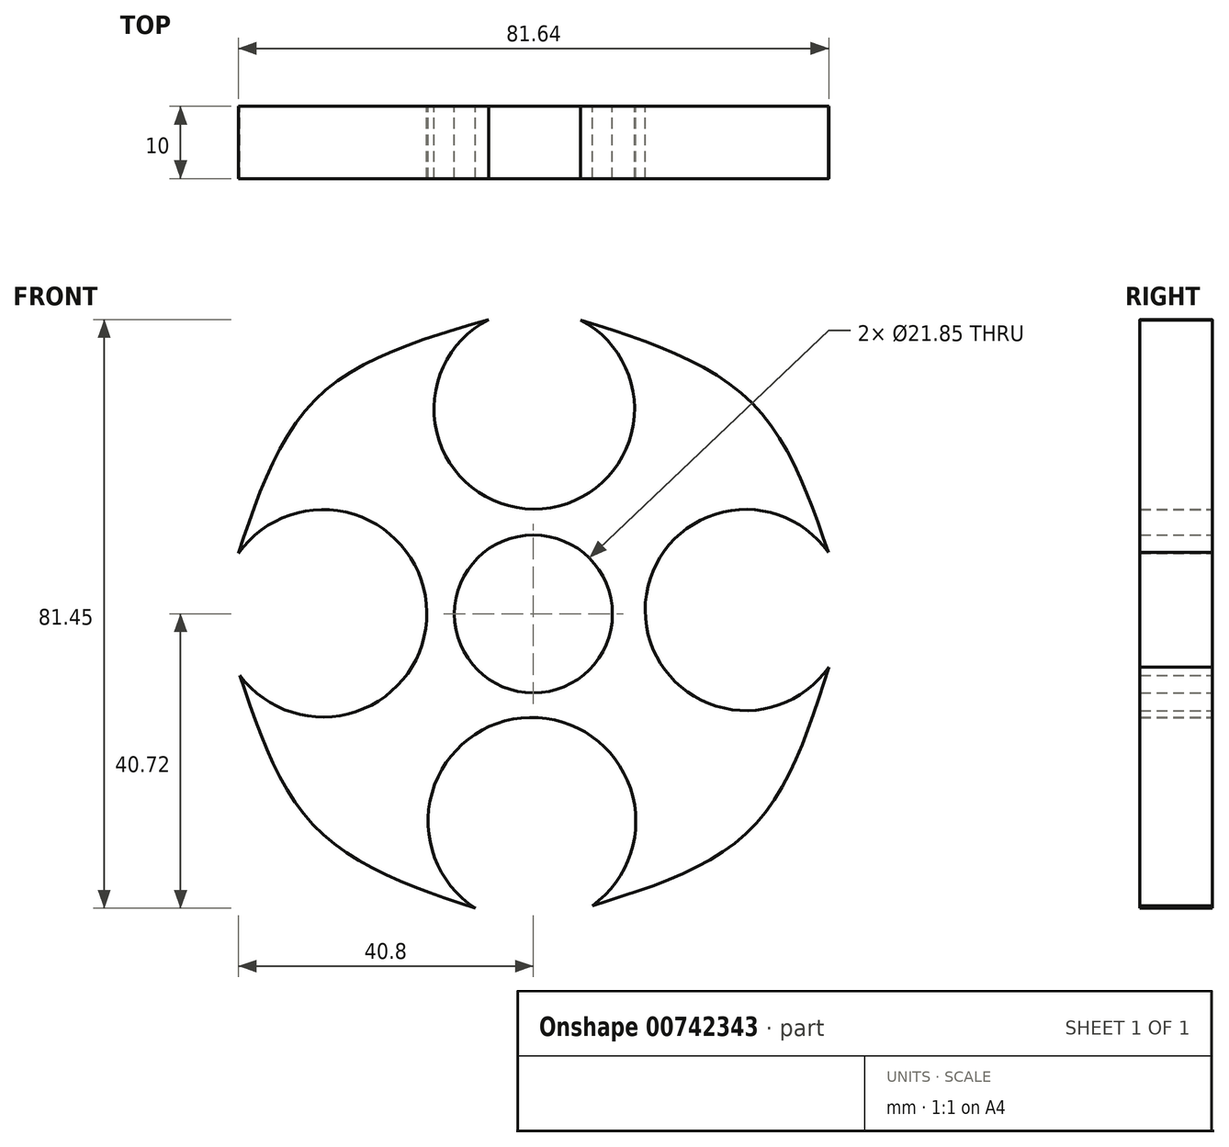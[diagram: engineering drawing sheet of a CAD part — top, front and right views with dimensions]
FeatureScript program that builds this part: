
annotation { "Feature Type Name" : "Feature", "Feature Type Description" : "" }
export const myFeature = defineFeature(function(context is Context, id is Id, definition is map)
    precondition{}
    {
        {
            var Q0;
            Q0=qCreatedBy(makeId("Front.planeOp"),FACE);
            var sketch = newSketch(context, id + "F0", { "sketchPlane" : qUnion([Q0])});
            skCircle(sketch, "E0", {"center": v(0, 0) * mm, "radius": 10.93 * mm});
            skArc(sketch, "E1", {"start": v(-6.18, 40.73) * mm, "mid": v(0.05, 14.5) * mm, "end": v(6.52, 40.66) * mm});
            skArc(sketch, "E2", {"start": v(8.15, -40.37) * mm, "mid": v(-0.52, -14.32) * mm, "end": v(-8.04, -40.72) * mm});
            skArc(sketch, "E3", {"start": v(40.78, 8.51) * mm, "mid": v(15.46, 0.49) * mm, "end": v(40.84, -7.33) * mm});
            skArc(sketch, "E4", {"start": v(-40.6, -8.47) * mm, "mid": v(-14.75, 0.25) * mm, "end": v(-40.8, 8.37) * mm});
            skFitSpline(sketch, "E5", {"points": [v(-40.8, 8.37) * mm, v(-29.74, 30.04) * mm, v(-6.18, 40.73) * mm], "startDerivative": vector(16.58, 49.68) * mm, "endDerivative": vector(52.5, 15.22) * mm});
            skFitSpline(sketch, "E6", {"points": [v(6.52, 40.66) * mm, v(29.89, 29.51) * mm, v(40.78, 8.51) * mm], "startDerivative": vector(51.69, -16.4) * mm, "endDerivative": vector(16.55, -48.15) * mm});
            skFitSpline(sketch, "E7", {"points": [v(40.84, -7.33) * mm, v(30, -29.82) * mm, v(8.15, -40.37) * mm], "startDerivative": vector(-15.89, -50.54) * mm, "endDerivative": vector(-49.57, -15.45) * mm});
            skFitSpline(sketch, "E8", {"points": [v(-8.04, -40.72) * mm, v(-29.9, -29.76) * mm, v(-40.6, -8.47) * mm], "startDerivative": vector(-48.92, 16.5) * mm, "endDerivative": vector(-16.14, 48.08) * mm});
            skSolve(sketch);
        }
        {
            var Q0;
            Q0=makeQuery(id+"F0.imprint","IMPRINT",FACE,{"disambiguationData":[TD([[makeQuery(id+"F0.imprint","IMPRINT",EDGE,{"derivedFrom":sQuery(id+"F0.wireOp",EDGE,"E0")}),-1.0]])]});
            var Q1;
            Q1 = qSketchRegion(id + "F0", true);
            extrude(context, id + "F1", {"entities" : qUnion([Q0, Q1]), "depth" : 10 * mm, "offsetDistance" : 25.4 * mm});
        }
    });
